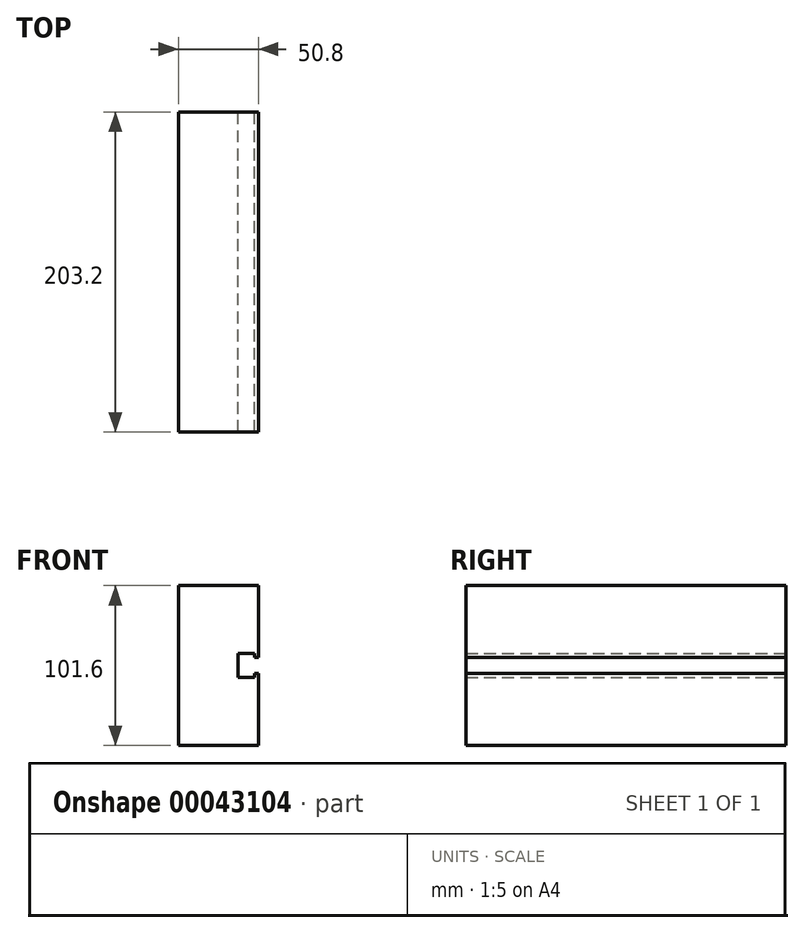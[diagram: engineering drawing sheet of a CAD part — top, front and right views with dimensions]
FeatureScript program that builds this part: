
annotation { "Feature Type Name" : "Feature", "Feature Type Description" : "" }
export const myFeature = defineFeature(function(context is Context, id is Id, definition is map)
    precondition{}
    {
        {
            var Q0;
            Q0=qCreatedBy(makeId("Front.planeOp"),FACE);
            var sketch = newSketch(context, id + "F0", { "sketchPlane" : qUnion([Q0])});
            skLineSegment(sketch, "E0.rect.bottom", {"start": v(25.4, -50.8) * mm, "end": v(-25.4, -50.8) * mm});
            skLineSegment(sketch, "E0.rect.top", {"start": v(25.4, 50.8) * mm, "end": v(-25.4, 50.8) * mm});
            skLineSegment(sketch, "E0.rect.right", {"start": v(-25.4, -50.8) * mm, "end": v(-25.4, 50.8) * mm});
            skPoint(sketch, "E0.rect.middle", {"position": v(0, 0) * mm});
            skLineSegment(sketch, "E1.bottom", {"start": v(25.4, 5.08) * mm, "end": v(22.86, 5.08) * mm});
            skLineSegment(sketch, "E2.top", {"start": v(22.86, 7.62) * mm, "end": v(12.7, 7.62) * mm});
            skLineSegment(sketch, "E2.right", {"start": v(12.7, 0) * mm, "end": v(12.7, 7.62) * mm});
            skLineSegment(sketch, "E3.MirrorCS", {"start": v(25.4, -5.08) * mm, "end": v(22.86, -5.08) * mm});
            skLineSegment(sketch, "E4.MirrorCS", {"start": v(12.7, 0) * mm, "end": v(12.7, -7.62) * mm});
            skLineSegment(sketch, "E5.MirrorCS", {"start": v(22.86, -7.62) * mm, "end": v(12.7, -7.62) * mm});
            skLineSegment(sketch, "E6", {"start": v(22.86, 7.62) * mm, "end": v(22.86, 5.08) * mm});
            skLineSegment(sketch, "E7", {"start": v(22.86, -7.62) * mm, "end": v(22.86, -5.08) * mm});
            skLineSegment(sketch, "E8", {"start": v(25.4, 50.8) * mm, "end": v(25.4, 5.08) * mm});
            skLineSegment(sketch, "E9", {"start": v(25.4, -5.08) * mm, "end": v(25.4, -50.8) * mm});
            skSolve(sketch);
        }
        {
            var Q0;
            Q0 = qSketchRegion(id + "F0", true);
            extrude(context, id + "F1", {"entities" : qUnion([Q0]), "depth" : 203.2 * mm});
        }
    });
